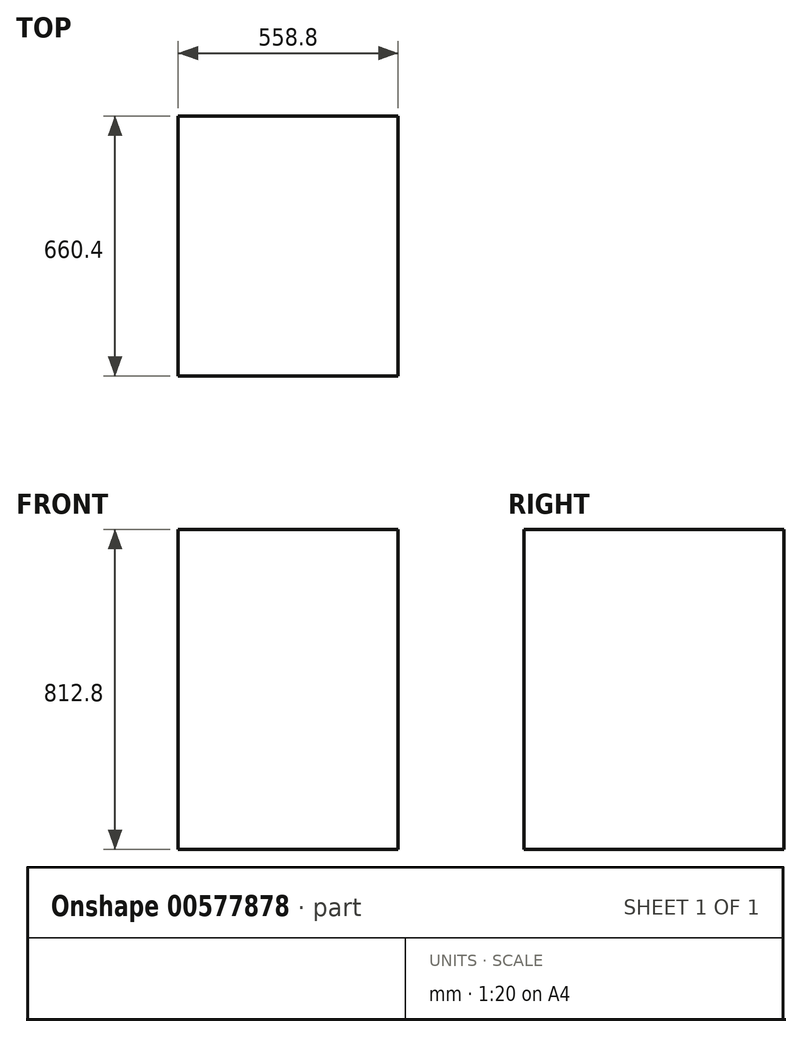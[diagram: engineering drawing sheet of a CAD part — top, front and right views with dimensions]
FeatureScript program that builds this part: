
annotation { "Feature Type Name" : "Feature", "Feature Type Description" : "" }
export const myFeature = defineFeature(function(context is Context, id is Id, definition is map)
    precondition{}
    {
        {
            var Q0;
            Q0=qCreatedBy(makeId("Top.planeOp"),FACE);
            var sketch = newSketch(context, id + "F0", { "sketchPlane" : qUnion([Q0])});
            skLineSegment(sketch, "E0.bottom", {"start": v(-279.4, -330.2) * mm, "end": v(279.4, -330.2) * mm});
            skLineSegment(sketch, "E0.top", {"start": v(-279.4, 330.2) * mm, "end": v(279.4, 330.2) * mm});
            skLineSegment(sketch, "E0.left", {"start": v(-279.4, -330.2) * mm, "end": v(-279.4, 330.2) * mm});
            skLineSegment(sketch, "E0.right", {"start": v(279.4, -330.2) * mm, "end": v(279.4, 330.2) * mm});
            skPoint(sketch, "E0.middle", {"position": v(0, 0) * mm});
            skSolve(sketch);
        }
        {
            var Q0;
            Q0=makeQuery(id+"F0.imprint","IMPRINT",FACE,{"disambiguationData":[TD([[makeQuery(id+"F0.imprint","IMPRINT",EDGE,{"derivedFrom":sQuery(id+"F0.wireOp",EDGE,"E0.bottom")}),1.0]])]});
            extrude(context, id + "F1", {"entities" : qUnion([Q0]), "oppositeDirection" : true, "depth" : 812.8 * mm, "offsetDistance" : 25.4 * mm});
        }
    });
